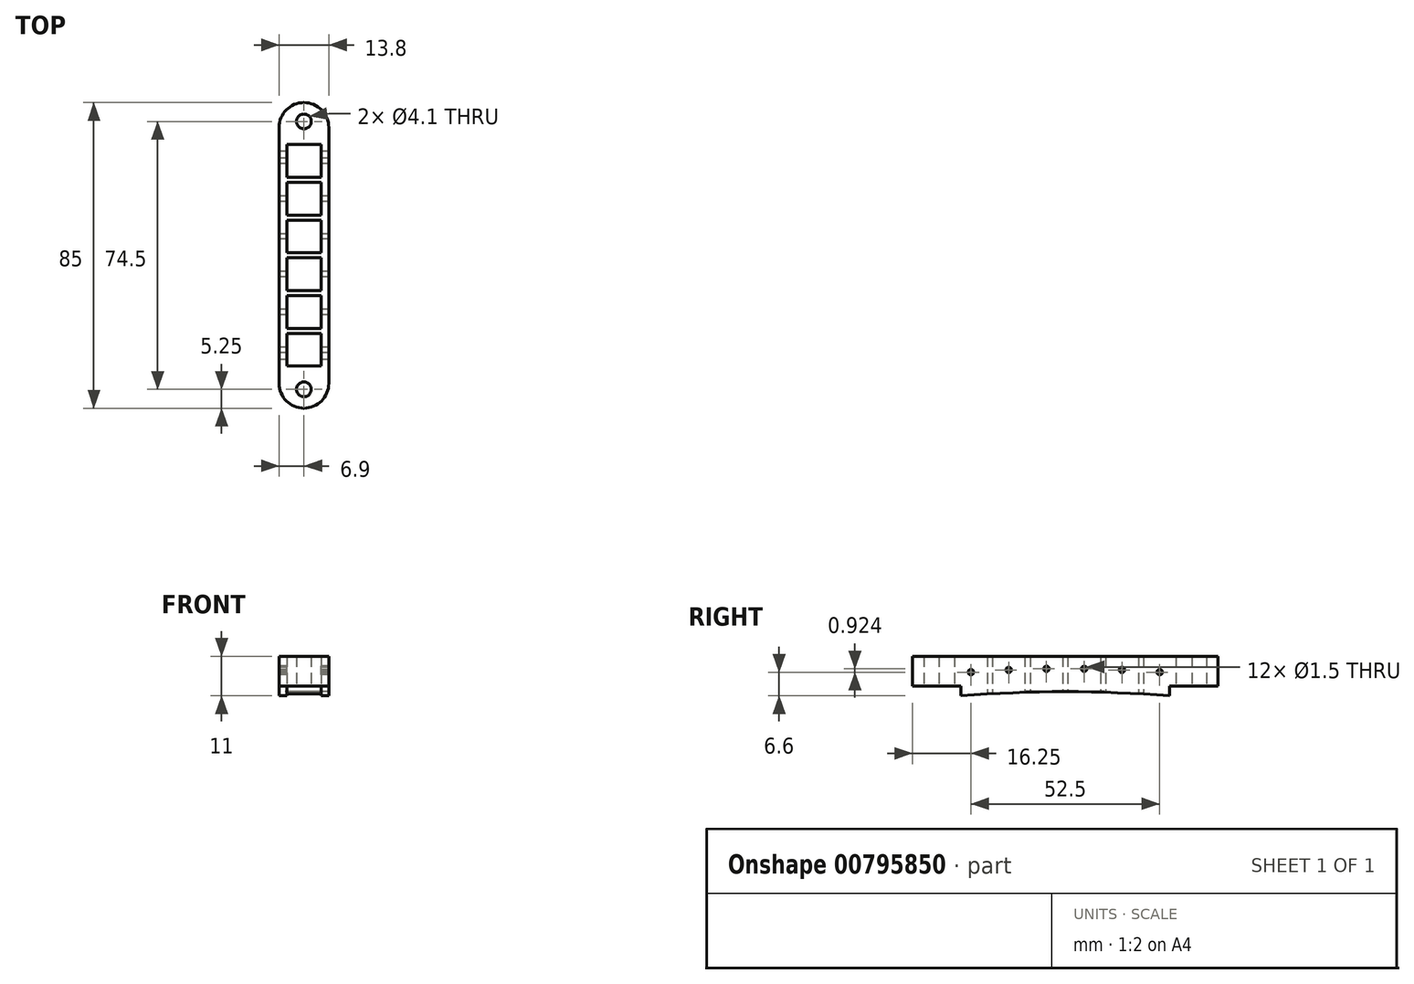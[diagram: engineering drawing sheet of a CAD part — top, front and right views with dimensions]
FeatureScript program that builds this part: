
annotation { "Feature Type Name" : "Feature", "Feature Type Description" : "" }
export const myFeature = defineFeature(function(context is Context, id is Id, definition is map)
    precondition{}
    {
        {
            var Q0;
            Q0=qCreatedBy(makeId("Top.planeOp"),FACE);
            var sketch = newSketch(context, id + "F0", { "sketchPlane" : qUnion([Q0])});
            skLineSegment(sketch, "E0.bottom", {"start": v(-6.9, 42.5) * mm, "end": v(6.9, 42.5) * mm, "construction": true});
            skLineSegment(sketch, "E0.top", {"start": v(-6.9, -42.5) * mm, "end": v(6.9, -42.5) * mm, "construction": true});
            skLineSegment(sketch, "E0.left", {"start": v(-6.9, 42.5) * mm, "end": v(-6.9, -42.5) * mm, "construction": true});
            skLineSegment(sketch, "E0.right", {"start": v(6.9, 42.5) * mm, "end": v(6.9, -42.5) * mm, "construction": true});
            skCircle(sketch, "E1", {"center": v(0, 37.25) * mm, "radius": 2.05 * mm});
            skCircle(sketch, "E2", {"center": v(0, -37.25) * mm, "radius": 2.05 * mm});
            skArc(sketch, "E3", {"start": v(-6.9, 35.6) * mm, "mid": v(0, 42.5) * mm, "end": v(6.9, 35.6) * mm});
            skArc(sketch, "E4", {"start": v(-6.9, -35.6) * mm, "mid": v(0, -42.5) * mm, "end": v(6.9, -35.6) * mm});
            skLineSegment(sketch, "E5", {"start": v(-6.9, 35.6) * mm, "end": v(-6.9, -35.6) * mm});
            skLineSegment(sketch, "E6", {"start": v(6.9, 35.6) * mm, "end": v(6.9, -35.6) * mm});
            skLineSegment(sketch, "E7.bottom", {"start": v(-4.8, 30.8) * mm, "end": v(4.8, 30.8) * mm});
            skLineSegment(sketch, "E7.top", {"start": v(-4.8, 21.7) * mm, "end": v(4.8, 21.7) * mm});
            skLineSegment(sketch, "E7.left", {"start": v(-4.8, 30.8) * mm, "end": v(-4.8, 21.7) * mm});
            skLineSegment(sketch, "E7.right", {"start": v(4.8, 30.8) * mm, "end": v(4.8, 21.7) * mm});
            skLineSegment(sketch, "E8.direction1", {"start": v(-4.8, 30.8) * mm, "end": v(20.2, 30.8) * mm, "construction": true});
            skLineSegment(sketch, "E8.direction2", {"start": v(-4.8, 30.8) * mm, "end": v(-4.8, 20.6) * mm, "construction": true});
            skLineSegment(sketch, "E9.0.1.0", {"start": v(-4.8, 20.3) * mm, "end": v(20.2, 20.3) * mm, "construction": true});
            skLineSegment(sketch, "E9.0.2.0", {"start": v(-4.8, 9.8) * mm, "end": v(20.2, 9.8) * mm, "construction": true});
            skLineSegment(sketch, "E9.0.3.0", {"start": v(-4.8, -0.7) * mm, "end": v(20.2, -0.7) * mm, "construction": true});
            skLineSegment(sketch, "E9.0.4.0", {"start": v(-4.8, -11.2) * mm, "end": v(20.2, -11.2) * mm, "construction": true});
            skLineSegment(sketch, "E9.0.5.0", {"start": v(-4.8, -21.7) * mm, "end": v(20.2, -21.7) * mm, "construction": true});
            skLineSegment(sketch, "E9.direction2", {"start": v(-4.8, 30.8) * mm, "end": v(-4.8, 20.3) * mm, "construction": true});
            skLineSegment(sketch, "E10.bottom", {"start": v(-4.8, -21.7) * mm, "end": v(4.8, -21.7) * mm});
            skLineSegment(sketch, "E10.top", {"start": v(-4.8, -30.8) * mm, "end": v(4.8, -30.8) * mm});
            skLineSegment(sketch, "E10.left", {"start": v(-4.8, -21.7) * mm, "end": v(-4.8, -30.8) * mm});
            skLineSegment(sketch, "E10.right", {"start": v(4.8, -21.7) * mm, "end": v(4.8, -30.8) * mm});
            skLineSegment(sketch, "E11.bottom", {"start": v(-4.8, 20.3) * mm, "end": v(4.8, 20.3) * mm});
            skLineSegment(sketch, "E11.top", {"start": v(-4.8, 11.2) * mm, "end": v(4.8, 11.2) * mm});
            skLineSegment(sketch, "E11.left", {"start": v(-4.8, 20.3) * mm, "end": v(-4.8, 11.2) * mm});
            skLineSegment(sketch, "E11.right", {"start": v(4.8, 20.3) * mm, "end": v(4.8, 11.2) * mm});
            skLineSegment(sketch, "E12.bottom", {"start": v(-4.8, 9.8) * mm, "end": v(4.8, 9.8) * mm});
            skLineSegment(sketch, "E12.top", {"start": v(-4.8, 0.7) * mm, "end": v(4.8, 0.7) * mm});
            skLineSegment(sketch, "E12.left", {"start": v(-4.8, 9.8) * mm, "end": v(-4.8, 0.7) * mm});
            skLineSegment(sketch, "E12.right", {"start": v(4.8, 9.8) * mm, "end": v(4.8, 0.7) * mm});
            skLineSegment(sketch, "E13.bottom", {"start": v(-4.8, -0.7) * mm, "end": v(4.8, -0.7) * mm});
            skLineSegment(sketch, "E13.top", {"start": v(-4.8, -9.8) * mm, "end": v(4.8, -9.8) * mm});
            skLineSegment(sketch, "E13.left", {"start": v(-4.8, -0.7) * mm, "end": v(-4.8, -9.8) * mm});
            skLineSegment(sketch, "E13.right", {"start": v(4.8, -0.7) * mm, "end": v(4.8, -9.8) * mm});
            skLineSegment(sketch, "E14.bottom", {"start": v(-4.8, -11.2) * mm, "end": v(4.8, -11.2) * mm});
            skLineSegment(sketch, "E14.top", {"start": v(-4.8, -20.3) * mm, "end": v(4.8, -20.3) * mm});
            skLineSegment(sketch, "E14.left", {"start": v(-4.8, -11.2) * mm, "end": v(-4.8, -20.3) * mm});
            skLineSegment(sketch, "E14.right", {"start": v(4.8, -11.2) * mm, "end": v(4.8, -20.3) * mm});
            skSolve(sketch);
        }
        {
            var Q0;
            Q0 = qSketchRegion(id + "F0", true);
            extrude(context, id + "F1", {"entities" : qUnion([Q0]), "depth" : 11 * mm, "offsetDistance" : 25 * mm});
        }
        {
            var Q0;
            Q0=makeQuery(id+"F1.opExtrude","SWEPT_FACE",FACE,{"disambiguationData":[OSD([sQuery(id+"F0.wireOp",EDGE,"E5")])]});
            var sketch = newSketch(context, id + "F2", { "sketchPlane" : qUnion([Q0])});
            skArc(sketch, "E15", {"start": v(-29, 0) * mm, "mid": v(0, 1.18) * mm, "end": v(29, 0) * mm});
            skLineSegment(sketch, "E16", {"start": v(29, 0) * mm, "end": v(29, 2.7) * mm});
            skLineSegment(sketch, "E17", {"start": v(29, 2.7) * mm, "end": v(42.5, 2.7) * mm});
            skLineSegment(sketch, "E18", {"start": v(42.5, 2.7) * mm, "end": v(42.5, 0) * mm});
            skLineSegment(sketch, "E19", {"start": v(42.5, 0) * mm, "end": v(-42.5, 0) * mm});
            skLineSegment(sketch, "E20", {"start": v(-42.5, 0) * mm, "end": v(-42.5, 2.7) * mm});
            skLineSegment(sketch, "E21", {"start": v(-42.5, 2.7) * mm, "end": v(-29, 2.7) * mm});
            skLineSegment(sketch, "E22", {"start": v(-29, 2.7) * mm, "end": v(-29, 0) * mm});
            skLineSegment(sketch, "E23", {"start": v(-42.5, 20.65) * mm, "end": v(-42.5, -9.06) * mm, "construction": true});
            skLineSegment(sketch, "E24", {"start": v(42.5, 26.99) * mm, "end": v(42.5, -13.15) * mm, "construction": true});
            skArc(sketch, "E25", {"start": v(-26.25, 6.6) * mm, "mid": v(0, 7.56) * mm, "end": v(26.25, 6.6) * mm, "construction": true});
            skLineSegment(sketch, "E26", {"start": v(-26.25, 11) * mm, "end": v(-26.25, 0) * mm, "construction": true});
            skCircle(sketch, "E27", {"center": v(-26.25, 6.6) * mm, "radius": 0.75 * mm});
            skCircle(sketch, "E28", {"center": v(-15.75, 7.22) * mm, "radius": 0.75 * mm});
            skCircle(sketch, "E29", {"center": v(-5.25, 7.52) * mm, "radius": 0.75 * mm});
            skCircle(sketch, "E30", {"center": v(5.25, 7.52) * mm, "radius": 0.75 * mm});
            skCircle(sketch, "E31", {"center": v(15.75, 7.22) * mm, "radius": 0.75 * mm});
            skCircle(sketch, "E32", {"center": v(26.25, 6.6) * mm, "radius": 0.75 * mm});
            skSolve(sketch);
        }
        {
            var Q0;
            Q0 = qSketchRegion(id + "F2", true);
            extrude(context, id + "F3", {"entities" : qUnion([Q0]), "operationType" : NewBodyOperationType.REMOVE, "endBound" : BoundingType.THROUGH_ALL, "oppositeDirection" : true, "depth" : 25 * mm, "offsetDistance" : 25 * mm});
        }
    });
